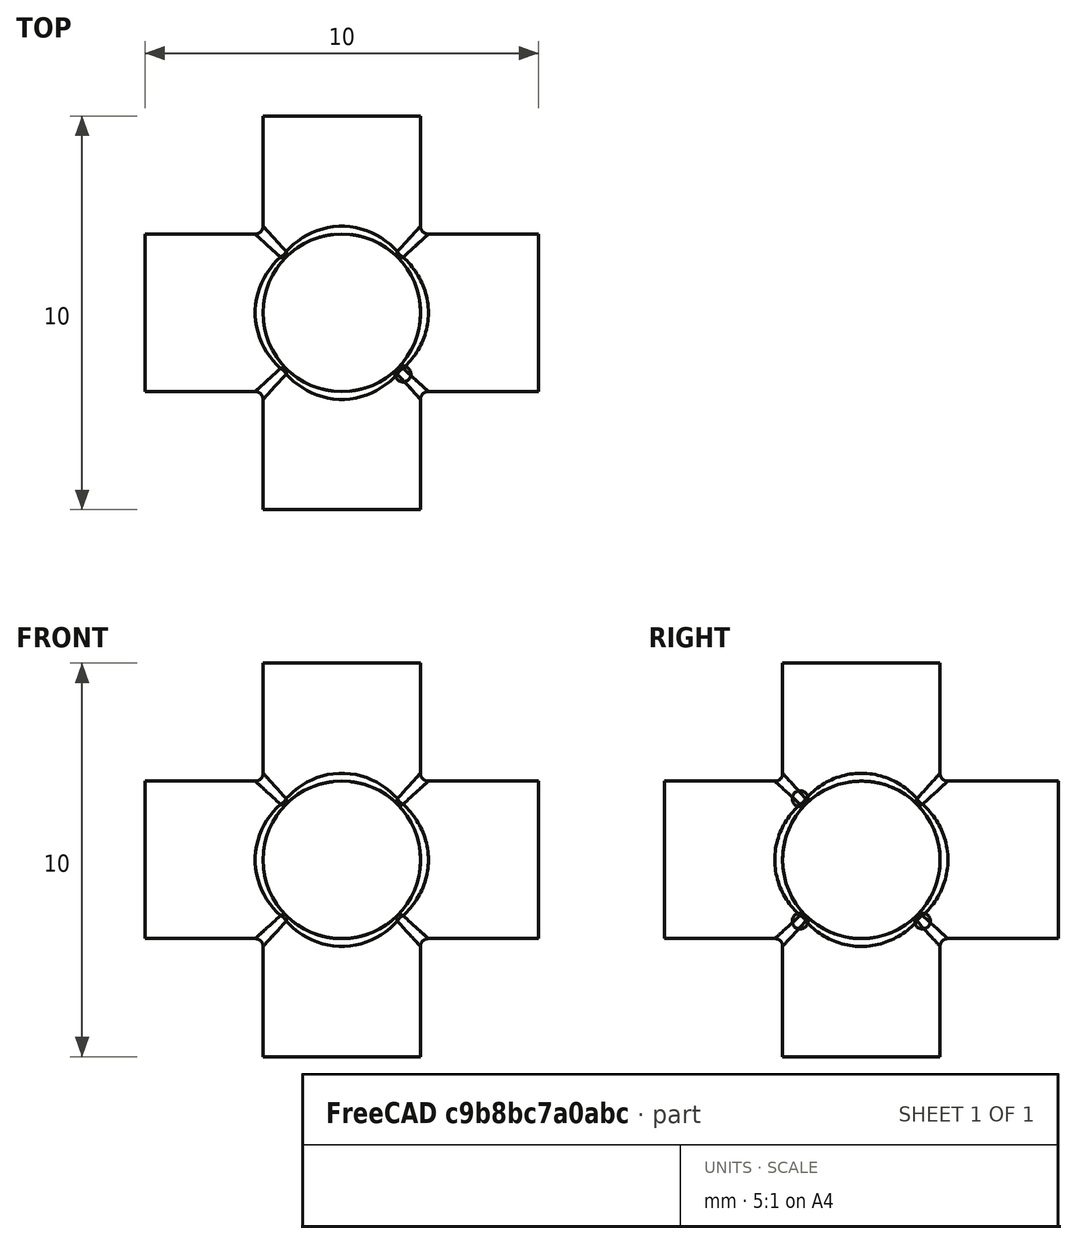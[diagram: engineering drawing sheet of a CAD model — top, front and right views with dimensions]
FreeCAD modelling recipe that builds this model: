
FCSTD DOCUMENT  (FreeCAD 0.21R33668 +26 (Git))
Label: testmodel
License: All rights reserved
LicenseURL: https://en.wikipedia.org/wiki/All_rights_reserved
objects: Part::Cylinder×3, Mesh::Feature×2, Part::MultiFuse×1, Part::Fillet×1
note: 5 computed .brp shape members not serialized (recipe doc carries the construction recipe); baked Part::Feature solids carry a one-line shape summary decoded from their .brp

FEATURE [Part::Cylinder] Cylinder  label="Цилиндр"
  Angle = 360
  AttacherType = Attacher::AttachEngine3D
  FirstAngle = 0
  Height = 10
  Placement = pos=(0,5,0) rot=(1,0,0;1.5708rad)
  Radius = 2
  SecondAngle = 0
FEATURE [Part::Cylinder] Cylinder001  label="Цилиндр001"
  Angle = 360
  AttacherType = Attacher::AttachEngine3D
  FirstAngle = 0
  Height = 10
  Placement = pos=(0,0,-5) rot=(0,0,1;0rad)
  Radius = 2
  SecondAngle = 0
FEATURE [Part::Cylinder] Cylinder002  label="Цилиндр002"
  Angle = 360
  AttacherType = Attacher::AttachEngine3D
  FirstAngle = 0
  Height = 10
  Placement = pos=(-5,0,0) rot=(0,1,0;1.5708rad)
  Radius = 2
  SecondAngle = 0
FEATURE [Part::MultiFuse] Fusion
  Shapes = -> [Cylinder,Cylinder001,Cylinder002]
FEATURE [Part::Fillet] Fillet
  Base = -> Fusion
  Edges = 20 edges r=0.2: [Edge3,Edge4,Edge5,Edge6,Edge7,Edge8,Edge9,Edge10,Edge11,Edge12,Edge13,Edge14,Edge15,Edge16,Edge21,Edge22,Edge23,Edge24,Edge25,Edge28]
FEATURE [Mesh::Feature] Mesh  label="Fillet (Meshed)"
FEATURE [Mesh::Feature] Mesh001  label="Fillet (Meshed)001"
